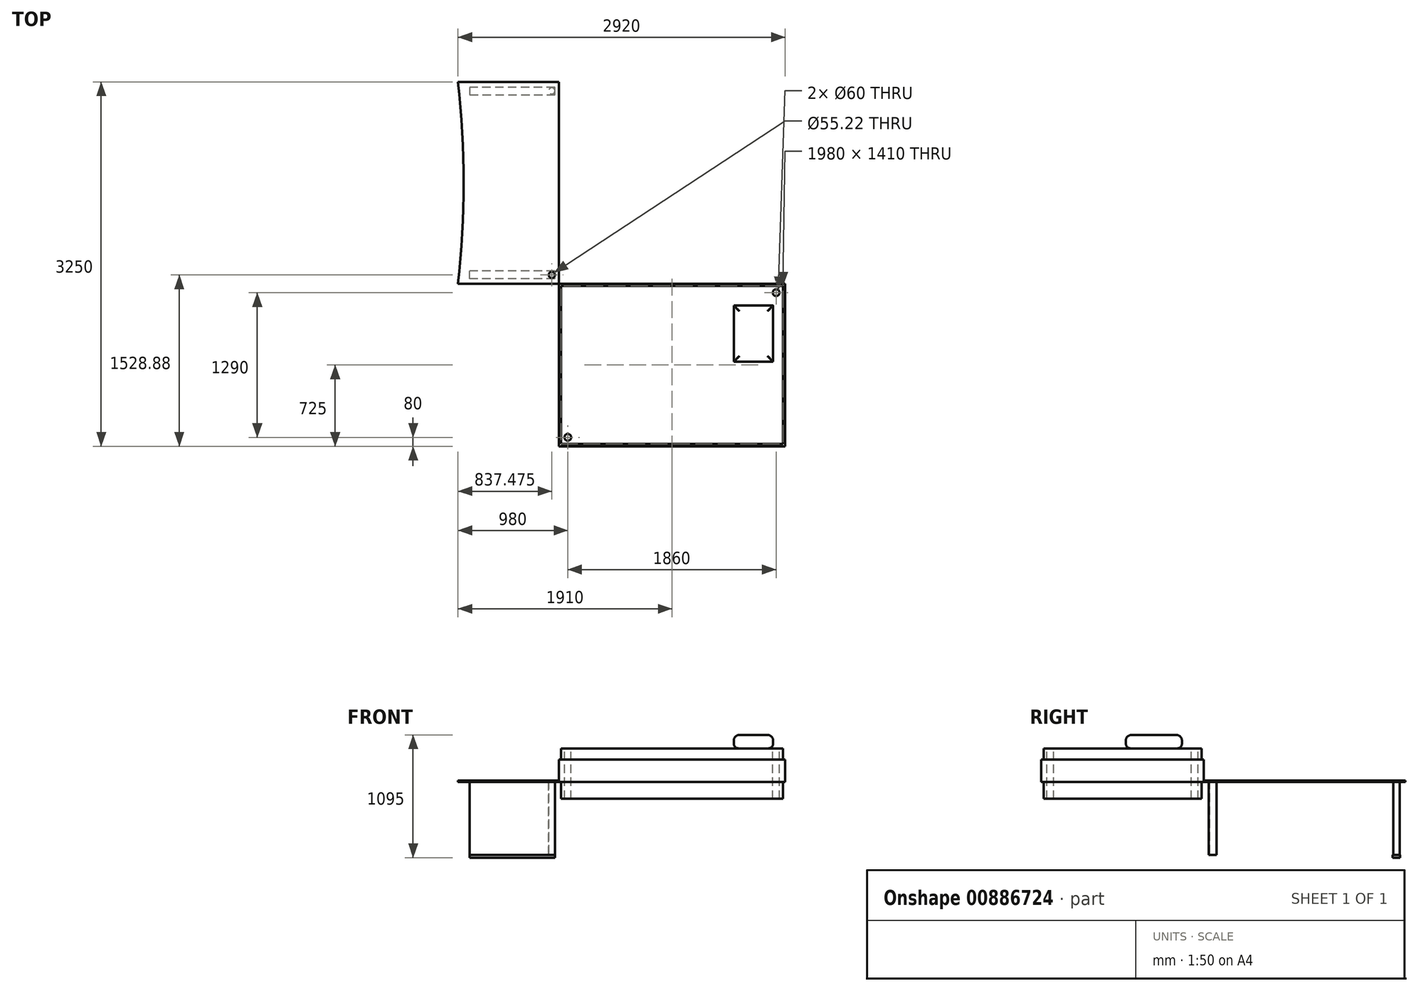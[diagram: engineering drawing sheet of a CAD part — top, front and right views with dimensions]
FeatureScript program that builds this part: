
annotation { "Feature Type Name" : "Feature", "Feature Type Description" : "" }
export const myFeature = defineFeature(function(context is Context, id is Id, definition is map)
    precondition{}
    {
        {
            var Q0;
            Q0=qCreatedBy(makeId("Top.planeOp"),FACE);
            var sketch = newSketch(context, id + "F0", { "sketchPlane" : qUnion([Q0])});
            skLineSegment(sketch, "E0.bottom", {"start": v(0, 0) * mm, "end": v(2020, 0) * mm});
            skLineSegment(sketch, "E0.top", {"start": v(0, -1450) * mm, "end": v(2020, -1450) * mm});
            skLineSegment(sketch, "E0.left", {"start": v(0, 0) * mm, "end": v(0, -1450) * mm});
            skLineSegment(sketch, "E0.right", {"start": v(2020, 0) * mm, "end": v(2020, -1450) * mm});
            skCircle(sketch, "E1", {"center": v(80, -80) * mm, "radius": 30 * mm});
            skLineSegment(sketch, "E2", {"start": v(1010, 0) * mm, "end": v(1010, -1450) * mm, "construction": true});
            skLineSegment(sketch, "E3", {"start": v(2020, -725) * mm, "end": v(0, -725) * mm, "construction": true});
            skCircle(sketch, "E4.MirrorC", {"center": v(1940, -80) * mm, "radius": 30 * mm});
            skCircle(sketch, "E5.MirrorC", {"center": v(80, -1370) * mm, "radius": 30 * mm});
            skCircle(sketch, "E6.MirrorC", {"center": v(1940, -1370) * mm, "radius": 30 * mm});
            skLineSegment(sketch, "E7.bottom", {"start": v(20, -20) * mm, "end": v(2000, -20) * mm});
            skLineSegment(sketch, "E7.top", {"start": v(20, -1430) * mm, "end": v(2000, -1430) * mm});
            skLineSegment(sketch, "E7.left", {"start": v(20, -20) * mm, "end": v(20, -1430) * mm});
            skLineSegment(sketch, "E7.right", {"start": v(2000, -20) * mm, "end": v(2000, -1430) * mm});
            skSolve(sketch);
        }
        {
            var Q0;
            Q0=makeQuery(id+"F0.imprint","IMPRINT",FACE,{"disambiguationData":[TD([[makeQuery(id+"F0.imprint","IMPRINT",EDGE,{"derivedFrom":sQuery(id+"F0.wireOp",EDGE,"E0.bottom")}),-1.0]])]});
            extrude(context, id + "F1", {"entities" : qUnion([Q0]), "depth" : 200 * mm, "offsetDistance" : 25 * mm});
        }
        {
            var Q0;
            Q0=makeQuery(id+"F0.imprint","IMPRINT",FACE,{"disambiguationData":[TD([[makeQuery(id+"F0.imprint","IMPRINT",EDGE,{"derivedFrom":sQuery(id+"F0.wireOp",EDGE,"E5.MirrorC")}),-1.0]])]});
            var Q1;
            Q1=makeQuery(id+"F0.imprint","IMPRINT",FACE,{"disambiguationData":[TD([[makeQuery(id+"F0.imprint","IMPRINT",EDGE,{"derivedFrom":sQuery(id+"F0.wireOp",EDGE,"E1")}),1.0]])]});
            var Q2;
            Q2=makeQuery(id+"F0.imprint","IMPRINT",FACE,{"disambiguationData":[TD([[makeQuery(id+"F0.imprint","IMPRINT",EDGE,{"derivedFrom":sQuery(id+"F0.wireOp",EDGE,"E6.MirrorC")}),1.0]])]});
            var Q3;
            Q3=makeQuery(id+"F0.imprint","IMPRINT",FACE,{"disambiguationData":[TD([[makeQuery(id+"F0.imprint","IMPRINT",EDGE,{"derivedFrom":sQuery(id+"F0.wireOp",EDGE,"E4.MirrorC")}),-1.0]])]});
            extrude(context, id + "F2", {"entities" : qUnion([Q0, Q1, Q2, Q3]), "operationType" : NewBodyOperationType.ADD, "oppositeDirection" : true, "depth" : 150 * mm, "offsetDistance" : 25 * mm});
        }
        {
            var Q0;
            Q0=makeQuery(id+"F0.imprint","IMPRINT",FACE,{"disambiguationData":[TD([[makeQuery(id+"F0.imprint","IMPRINT",EDGE,{"derivedFrom":sQuery(id+"F0.wireOp",EDGE,"E1")}),-1.0]])]});
            var Q1;
            Q1=makeQuery(id+"F0.imprint","IMPRINT",FACE,{"disambiguationData":[TD([[makeQuery(id+"F0.imprint","IMPRINT",EDGE,{"derivedFrom":sQuery(id+"F0.wireOp",EDGE,"E6.MirrorC")}),1.0]])]});
            var Q2;
            Q2=makeQuery(id+"F0.imprint","IMPRINT",FACE,{"disambiguationData":[TD([[makeQuery(id+"F0.imprint","IMPRINT",EDGE,{"derivedFrom":sQuery(id+"F0.wireOp",EDGE,"E4.MirrorC")}),-1.0]])]});
            var Q3;
            Q3=makeQuery(id+"F0.imprint","IMPRINT",FACE,{"disambiguationData":[TD([[makeQuery(id+"F0.imprint","IMPRINT",EDGE,{"derivedFrom":sQuery(id+"F0.wireOp",EDGE,"E1")}),1.0]])]});
            var Q4;
            Q4=makeQuery(id+"F0.imprint","IMPRINT",FACE,{"disambiguationData":[TD([[makeQuery(id+"F0.imprint","IMPRINT",EDGE,{"derivedFrom":sQuery(id+"F0.wireOp",EDGE,"E5.MirrorC")}),-1.0]])]});
            extrude(context, id + "F3", {"entities" : qUnion([Q0, Q1, Q2, Q3, Q4]), "operationType" : NewBodyOperationType.ADD, "depth" : 300 * mm, "offsetDistance" : 25 * mm});
        }
        {
            var Q0;
            Q0=makeQuery(id+"F3.opExtrude","CAP_FACE",FACE,{"disambiguationData":[OSD([sQuery(id+"F0.wireOp",EDGE,"E7.bottom"),sQuery(id+"F0.wireOp",EDGE,"E7.top"),sQuery(id+"F0.wireOp",EDGE,"E7.left"),sQuery(id+"F0.wireOp",EDGE,"E7.right")])],"isStart":false});
            var sketch = newSketch(context, id + "F4", { "sketchPlane" : qUnion([Q0])});
            skLineSegment(sketch, "E8.bottom", {"start": v(1562.38, -194.86) * mm, "end": v(1912.38, -194.86) * mm});
            skLineSegment(sketch, "E8.top", {"start": v(1562.38, -694.86) * mm, "end": v(1912.38, -694.86) * mm});
            skLineSegment(sketch, "E8.left", {"start": v(1562.38, -194.86) * mm, "end": v(1562.38, -694.86) * mm});
            skLineSegment(sketch, "E8.right", {"start": v(1912.38, -194.86) * mm, "end": v(1912.38, -694.86) * mm});
            skSolve(sketch);
        }
        {
            var Q0;
            Q0=makeQuery(id+"F4.imprint","IMPRINT",FACE,{"disambiguationData":[TD([[makeQuery(id+"F4.imprint","IMPRINT",EDGE,{"derivedFrom":sQuery(id+"F4.wireOp",EDGE,"E8.bottom")}),-1.0]])]});
            extrude(context, id + "F5", {"entities" : qUnion([Q0]), "depth" : 120 * mm, "offsetDistance" : 25 * mm});
        }
        {
            var Q0;
            Q0=makeQuery(id+"F5.opExtrude","CAP_EDGE",EDGE,{"disambiguationData":[OSD([sQuery(id+"F4.wireOp",EDGE,"E8.left")])],"isStart":false});
            var Q1;
            Q1=makeQuery(id+"F5.opExtrude","CAP_EDGE",EDGE,{"disambiguationData":[OSD([sQuery(id+"F4.wireOp",EDGE,"E8.top")])],"isStart":false});
            var Q2;
            Q2=makeQuery(id+"F5.opExtrude","CAP_EDGE",EDGE,{"disambiguationData":[OSD([sQuery(id+"F4.wireOp",EDGE,"E8.right")])],"isStart":false});
            var Q3;
            Q3=makeQuery(id+"F5.opExtrude","CAP_EDGE",EDGE,{"disambiguationData":[OSD([sQuery(id+"F4.wireOp",EDGE,"E8.bottom")])],"isStart":false});
            fillet(context, id + "F6", {"entities" : qUnion([Q0, Q1, Q2, Q3]), "radius" : 50 * mm, "tangentPropagation" : true, "allowEdgeOverflow" : false});
        }
        {
            var Q0;
            Q0=makeQuery(id+"F5.opExtrude","CAP_EDGE",EDGE,{"disambiguationData":[OSD([sQuery(id+"F4.wireOp",EDGE,"E8.top")])],"isStart":true});
            var Q1;
            Q1=makeQuery(id+"F5.opExtrude","CAP_EDGE",EDGE,{"disambiguationData":[OSD([sQuery(id+"F4.wireOp",EDGE,"E8.left")])],"isStart":true});
            var Q2;
            Q2=makeQuery(id+"F5.opExtrude","CAP_EDGE",EDGE,{"disambiguationData":[OSD([sQuery(id+"F4.wireOp",EDGE,"E8.right")])],"isStart":true});
            var Q3;
            Q3=makeQuery(id+"F5.opExtrude","CAP_EDGE",EDGE,{"disambiguationData":[OSD([sQuery(id+"F4.wireOp",EDGE,"E8.bottom")])],"isStart":true});
            fillet(context, id + "F7", {"entities" : qUnion([Q0, Q1, Q2, Q3]), "radius" : 40 * mm, "tangentPropagation" : true, "allowEdgeOverflow" : false});
        }
        {
            var Q0;
            Q0=qCreatedBy(makeId("Top.planeOp"),FACE);
            var sketch = newSketch(context, id + "F8", { "sketchPlane" : qUnion([Q0])});
            skLineSegment(sketch, "E9.bottom", {"start": v(0, 0) * mm, "end": v(-900, 0) * mm});
            skLineSegment(sketch, "E9.top", {"start": v(0, 1800) * mm, "end": v(-900, 1800) * mm});
            skLineSegment(sketch, "E9.left", {"start": v(0, 0) * mm, "end": v(0, 1800) * mm});
            skLineSegment(sketch, "E9.right", {"start": v(-900, 0) * mm, "end": v(-900, 1800) * mm, "construction": true});
            skArc(sketch, "E10", {"start": v(-900, 0) * mm, "mid": v(-850, 900) * mm, "end": v(-900, 1800) * mm});
            skLineSegment(sketch, "E11", {"start": v(0, 900) * mm, "end": v(-850, 900) * mm, "construction": true});
            skLineSegment(sketch, "E12.bottom", {"start": v(-33.92, 1754.22) * mm, "end": v(-795.85, 1754.22) * mm});
            skLineSegment(sketch, "E12.top", {"start": v(-33.92, 1684.96) * mm, "end": v(-795.85, 1684.96) * mm});
            skLineSegment(sketch, "E12.left", {"start": v(-33.92, 1754.22) * mm, "end": v(-33.92, 1684.96) * mm});
            skLineSegment(sketch, "E12.right", {"start": v(-795.85, 1754.22) * mm, "end": v(-795.85, 1684.96) * mm});
            skLineSegment(sketch, "E13.MirrorCS", {"start": v(-795.85, 45.78) * mm, "end": v(-795.85, 115.04) * mm});
            skLineSegment(sketch, "E14.MirrorCS", {"start": v(-33.92, 45.78) * mm, "end": v(-795.85, 45.78) * mm});
            skLineSegment(sketch, "E15.MirrorCS", {"start": v(-33.92, 115.04) * mm, "end": v(-795.85, 115.04) * mm});
            skLineSegment(sketch, "E16.MirrorCS", {"start": v(-33.92, 45.78) * mm, "end": v(-33.92, 115.04) * mm});
            skCircle(sketch, "E17", {"center": v(-62.53, 1721.12) * mm, "radius": 27.6 * mm});
            skCircle(sketch, "E18.MirrorC", {"center": v(-62.53, 78.88) * mm, "radius": 27.6 * mm});
            skSolve(sketch);
        }
        {
            var Q0;
            Q0=makeQuery(id+"F8.imprint","IMPRINT",FACE,{"disambiguationData":[TD([[makeQuery(id+"F8.imprint","IMPRINT",EDGE,{"derivedFrom":sQuery(id+"F8.wireOp",EDGE,"E9.bottom")}),-1.0]])]});
            var Q1;
            Q1=makeQuery(id+"F8.imprint","IMPRINT",FACE,{"disambiguationData":[TD([[makeQuery(id+"F8.imprint","IMPRINT",EDGE,{"derivedFrom":sQuery(id+"F8.wireOp",EDGE,"E12.bottom")}),1.0]])]});
            var Q2;
            Q2=makeQuery(id+"F8.imprint","IMPRINT",FACE,{"disambiguationData":[TD([[makeQuery(id+"F8.imprint","IMPRINT",EDGE,{"derivedFrom":sQuery(id+"F8.wireOp",EDGE,"E17")}),1.0]])]});
            var Q3;
            Q3=makeQuery(id+"F8.imprint","IMPRINT",FACE,{"disambiguationData":[TD([[makeQuery(id+"F8.imprint","IMPRINT",EDGE,{"derivedFrom":sQuery(id+"F8.wireOp",EDGE,"E18.MirrorC")}),-1.0]])]});
            var Q4;
            Q4=makeQuery(id+"F8.imprint","IMPRINT",FACE,{"disambiguationData":[TD([[makeQuery(id+"F8.imprint","IMPRINT",EDGE,{"derivedFrom":sQuery(id+"F8.wireOp",EDGE,"E13.MirrorCS")}),-1.0]])]});
            extrude(context, id + "F9", {"entities" : qUnion([Q0, Q1, Q2, Q3, Q4]), "depth" : 12 * mm, "offsetDistance" : 25 * mm});
        }
        {
            var Q0;
            Q0=makeQuery(id+"F8.imprint","IMPRINT",FACE,{"disambiguationData":[TD([[makeQuery(id+"F8.imprint","IMPRINT",EDGE,{"derivedFrom":sQuery(id+"F8.wireOp",EDGE,"E17")}),1.0]])]});
            var Q1;
            Q1=makeQuery(id+"F8.imprint","IMPRINT",FACE,{"disambiguationData":[TD([[makeQuery(id+"F8.imprint","IMPRINT",EDGE,{"derivedFrom":sQuery(id+"F8.wireOp",EDGE,"E18.MirrorC")}),-1.0]])]});
            extrude(context, id + "F10", {"entities" : qUnion([Q0, Q1]), "operationType" : NewBodyOperationType.ADD, "oppositeDirection" : true, "depth" : 650 * mm, "offsetDistance" : 25 * mm});
        }
        {
            var Q0;
            Q0=makeQuery(id+"F10.opExtrude","CAP_FACE",FACE,{"disambiguationData":[OSD([sQuery(id+"F8.wireOp",EDGE,"E17")])],"isStart":false});
            var sketch = newSketch(context, id + "F11", { "sketchPlane" : qUnion([Q0])});
            skLineSegment(sketch, "E19.0.0", {"start": v(-795.85, -1684.96) * mm, "end": v(-33.92, -1684.96) * mm});
            skLineSegment(sketch, "E19.0.1", {"start": v(-33.92, -1684.96) * mm, "end": v(-33.92, -1754.22) * mm});
            skLineSegment(sketch, "E19.0.2", {"start": v(-33.92, -1754.22) * mm, "end": v(-795.85, -1754.22) * mm});
            skLineSegment(sketch, "E19.0.3", {"start": v(-795.85, -1754.22) * mm, "end": v(-795.85, -1684.96) * mm});
            skLineSegment(sketch, "E20.0", {"start": v(-33.92, -45.78) * mm, "end": v(-795.85, -45.78) * mm});
            skLineSegment(sketch, "E21.0.0", {"start": v(-795.85, -45.78) * mm, "end": v(-33.92, -45.78) * mm});
            skLineSegment(sketch, "E21.0.1", {"start": v(-33.92, -45.78) * mm, "end": v(-33.92, -115.04) * mm});
            skLineSegment(sketch, "E21.0.2", {"start": v(-33.92, -115.04) * mm, "end": v(-795.85, -115.04) * mm});
            skLineSegment(sketch, "E21.0.3", {"start": v(-795.85, -115.04) * mm, "end": v(-795.85, -45.78) * mm});
            skSolve(sketch);
        }
        {
            var Q0;
            Q0=makeQuery(id+"F11.imprint","IMPRINT",FACE,{"disambiguationData":[TD([[makeQuery(id+"F11.imprint","IMPRINT",EDGE,{"derivedFrom":sQuery(id+"F11.wireOp",EDGE,"E19.0.0")}),-1.0]])]});
            var Q1;
            Q1=makeQuery(id+"F11.imprint","IMPRINT",FACE,{"disambiguationData":[TD([[makeQuery(id+"F11.imprint","IMPRINT",EDGE,{"derivedFrom":sQuery(id+"F11.wireOp",EDGE,"E21.0.0")}),-1.0]])]});
            var Q2;
            Q2=makeQuery(id+"F11.imprint","IMPRINT",FACE,{"disambiguationData":[TD([[makeQuery(id+"F11.imprint","IMPRINT",EDGE,{"derivedFrom":makeQuery(id+"F10.opExtrude","CAP_EDGE",EDGE,{"disambiguationData":[OSD([sQuery(id+"F8.wireOp",EDGE,"E17")])],"isStart":false})}),-1.0]])]});
            extrude(context, id + "F12", {"entities" : qUnion([Q0, Q1, Q2]), "operationType" : NewBodyOperationType.ADD, "depth" : 25 * mm, "offsetDistance" : 25 * mm});
        }
    });
